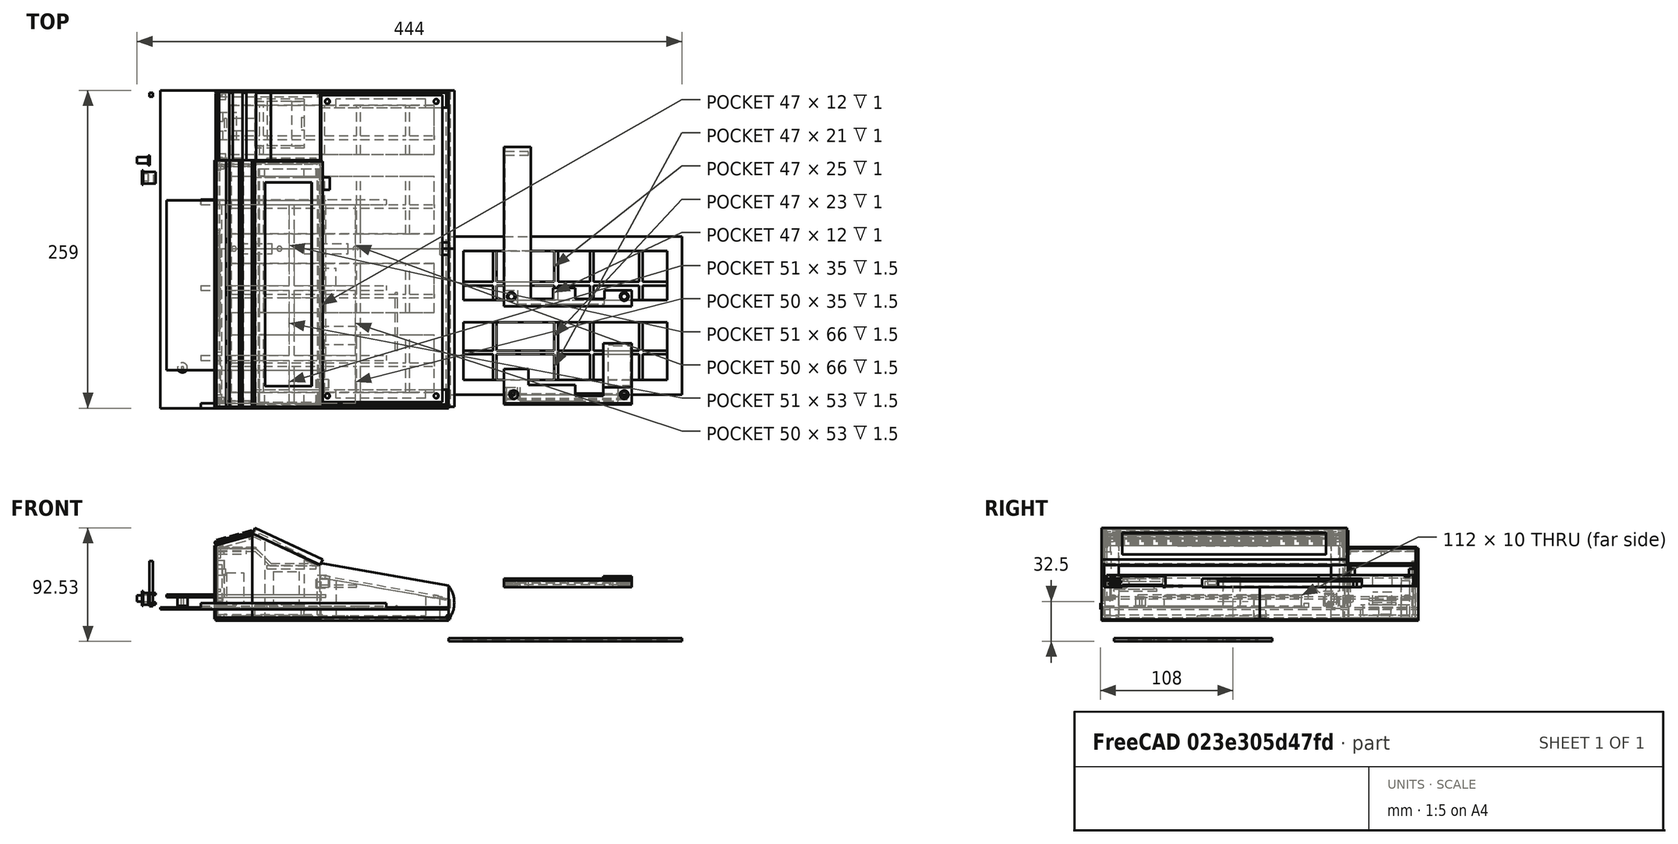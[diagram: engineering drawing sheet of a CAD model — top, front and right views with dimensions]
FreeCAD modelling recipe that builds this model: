
FCSTD DOCUMENT  (FreeCAD 0.20R29603 (Git))
Label: megav2
License: All rights reserved
LicenseURL: http://en.wikipedia.org/wiki/All_rights_reserved
objects: Part::Box×199, Part::Cut×81, Part::Cylinder×32, Part::MultiFuse×26, App::DocumentObjectGroup×14, Part::FeaturePython×1
note: 339 computed .brp shape members not serialized (recipe doc carries the construction recipe); baked Part::Feature solids carry a one-line shape summary decoded from their .brp

FEATURE [Part::Box] Box  label="5x50Keyboard"
  AttacherType = Attacher::AttachEngine3D
  Height = 2
  Length = 100
  Width = 250
FEATURE [Part::Box] Box001  label="MainBoardPCB"
  AttacherType = Attacher::AttachEngine3D
  Height = 2
  Length = 130
  Placement = pos=(-125,28,-8) rot=(0,0,1;0rad)
  Width = 138.5
FEATURE [Part::Box] Box002  label="4x40lcd"
  AttacherType = Attacher::AttachEngine3D
  Height = 2
  Length = 54
  Placement = pos=(-56,2,30) rot=(0,1,0;0.296706rad)
  Width = 190
FEATURE [Part::Box] Box050  label="Cube028"
  AttacherType = Attacher::AttachEngine3D
  Height = 9.5
  Length = 11
  Placement = pos=(0,0,35) rot=(0,0,1;0rad)
  Width = 9.5
FEATURE [Part::Box] Box051  label="Cube029"
  AttacherType = Attacher::AttachEngine3D
  Height = 12
  Length = 1
  Placement = pos=(0,-1,34) rot=(0,0,1;0rad)
  Width = 12
FEATURE [Part::Box] Box052  label="Cube030"
  AttacherType = Attacher::AttachEngine3D
  Height = 7.5
  Length = 4.5
  Placement = pos=(5,-1,36) rot=(0,0,1;0rad)
  Width = 13
FEATURE [Part::Box] Box053  label="Cube031"
  AttacherType = Attacher::AttachEngine3D
  Height = 6
  Length = 4.5
  Placement = pos=(9,-1,36.75) rot=(0,0,1;0rad)
  Width = 13
FEATURE [Part::Cylinder] Cylinder008
  Angle = 360
  AttacherType = Attacher::AttachEngine3D
  FirstAngle = 0
  Height = 9
  Placement = pos=(-1,5,40) rot=(0,1,0;1.5708rad)
  Radius = 3
  SecondAngle = 0
FEATURE [Part::MultiFuse] Fusion010
  Shapes = -> [Box050,Box051]
FEATURE [Part::Cut] Cut016
  Base = -> Fusion010
  Tool = -> Cylinder008
FEATURE [Part::Cut] Cut017
  Base = -> Cut016
  Tool = -> Box052
FEATURE [Part::Cut] Cut018
  Base = -> Cut017
  Placement = pos=(-145,180,-49) rot=(0,0,1;0rad)
  Tool = -> Box053
FEATURE [App::DocumentObjectGroup] Group007  label="resetbutton-case"
  Group = -> [Cut018]
FEATURE [Part::Box] Box054  label="Cube002"
  AttacherType = Attacher::AttachEngine3D
  Height = 60
  Length = 1.5
  Placement = pos=(0,0,-19.5) rot=(0,0,1;0rad)
  Width = 194
FEATURE [Part::Box] Box004  label="Cube003"
  AttacherType = Attacher::AttachEngine3D
  Height = 10
  Length = 10
  Placement = pos=(-3,48,-10) rot=(0,0,1;0rad)
  Width = 112
FEATURE [Part::Box] Box021  label="reset"
  AttacherType = Attacher::AttachEngine3D
  Height = 10
  Length = 10
  Placement = pos=(-2,175,0) rot=(0,0,1;0rad)
  Width = 10
FEATURE [Part::Box] Box025  label="Cube004"
  AttacherType = Attacher::AttachEngine3D
  Height = 5
  Length = 4
  Placement = pos=(1,0,35.5) rot=(0,0,1;0rad)
  Width = 4
FEATURE [Part::Box] Box026  label="Cube005"
  AttacherType = Attacher::AttachEngine3D
  Height = 10
  Length = 4
  Placement = pos=(1,190,30.5) rot=(0,0,1;0rad)
  Width = 4
FEATURE [Part::Cylinder] Cylinder004  label="pwrjack"
  Angle = 360
  AttacherType = Attacher::AttachEngine3D
  FirstAngle = 0
  Height = 10
  Placement = pos=(-3,17,3) rot=(0,1,0;1.5708rad)
  Radius = 3.5
  SecondAngle = 0
FEATURE [Part::Box] Box055  label="Cube032"
  AttacherType = Attacher::AttachEngine3D
  Height = 5.5
  Length = 1.5
  Placement = pos=(7,1,37) rot=(0,0,1;0rad)
  Width = 8
FEATURE [Part::Cylinder] Cylinder009
  Angle = 360
  AttacherType = Attacher::AttachEngine3D
  FirstAngle = 0
  Height = 10
  Placement = pos=(-2,5,40) rot=(0,1,0;1.5708rad)
  Radius = 2.5
  SecondAngle = 0
FEATURE [Part::MultiFuse] Fusion012
  Placement = pos=(-147,194,-49) rot=(0,0,1;0rad)
  Shapes = -> [Cylinder009,Box055]
FEATURE [App::DocumentObjectGroup] Group008  label="resetbutton"
  Group = -> [Fusion012]
FEATURE [Part::Box] Box056  label="base"
  AttacherType = Attacher::AttachEngine3D
  Height = 1.5
  Length = 235
  Placement = pos=(-25,0,-10) rot=(1,0,0;0rad)
  Width = 259
FEATURE [Part::Box] Box027  label="Cube006"
  AttacherType = Attacher::AttachEngine3D
  Height = 4
  Length = 151
  Placement = pos=(8,0,-9) rot=(0,0,1;0rad)
  Width = 4
FEATURE [Part::Box] Box028  label="Cube007"
  AttacherType = Attacher::AttachEngine3D
  Height = 4
  Length = 151
  Placement = pos=(8,166,-9) rot=(0,0,1;0rad)
  Width = 4
FEATURE [Part::Box] Box029  label="Face003"
  AttacherType = Attacher::AttachEngine3D
  Height = 55
  Length = 2
  Placement = pos=(169.2,0,-11) rot=(0,-1,0;0.261799rad)
  Width = 254
FEATURE [Part::Box] Box036  label="Cube014"
  AttacherType = Attacher::AttachEngine3D
  Height = 2
  Length = 151
  Placement = pos=(8,96,-9) rot=(0,0,1;0rad)
  Width = 4
FEATURE [Part::Box] Box037  label="Cube015"
  AttacherType = Attacher::AttachEngine3D
  Height = 2
  Length = 151
  Placement = pos=(8,39,-9) rot=(0,0,1;0rad)
  Width = 4
FEATURE [Part::Box] Box038  label="Cube016"
  AttacherType = Attacher::AttachEngine3D
  Height = 2
  Length = 170
  Placement = pos=(29,0,-9) rot=(0,0,1;1.5708rad)
  Width = 4
FEATURE [Part::Box] Box039  label="Cube017"
  AttacherType = Attacher::AttachEngine3D
  Height = 2
  Length = 170
  Placement = pos=(84,0,-9) rot=(0,0,1;1.5708rad)
  Width = 4
FEATURE [Part::Box] Box040  label="Cube018"
  AttacherType = Attacher::AttachEngine3D
  Height = 2
  Length = 170
  Placement = pos=(138,0,-9) rot=(0,0,1;1.5708rad)
  Width = 4
FEATURE [Part::Cylinder] Cylinder007
  Angle = 360
  AttacherType = Attacher::AttachEngine3D
  FirstAngle = 0
  Height = 47
  Placement = pos=(167.4,94,-8.1) rot=(1,0,0;1.5708rad)
  Radius = 1
  SecondAngle = 0
FEATURE [Part::MultiFuse] Fusion005
  Shapes = -> [Box027,Box028]
FEATURE [Part::Cut] Cut009
  Base = -> Fusion005
  Tool = -> Box029
FEATURE [Part::MultiFuse] Fusion006
  Placement = pos=(-105,-3,-8) rot=(0,0,1;0rad)
  Refine = true
  Shapes = -> [Cut009,Cylinder007,Box036,Box037,Box038,Box039,Box040,Box056]
FEATURE [App::DocumentObjectGroup] Group009  label="CaseBaseold"
  Group = -> [Fusion006]
FEATURE [Part::FeaturePython] Tube002  label="PCBFoot"  # WARN: FeaturePython — macro-defined, semantics opaque (R4)
  AttacherType = Attacher::AttachEngine3D
  Height = 7
  InnerRadius = 1
  OuterRadius = 4
  Placement = pos=(-112,30,-15) rot=(0,0,1;0rad)
FEATURE [Part::Cylinder] Cylinder010
  Angle = 360
  AttacherType = Attacher::AttachEngine3D
  FirstAngle = 0
  Height = 20
  Placement = pos=(5,5,-2) rot=(0,0,1;0rad)
  Radius = 2
  SecondAngle = 0
FEATURE [Part::Cylinder] Cylinder011
  Angle = 360
  AttacherType = Attacher::AttachEngine3D
  FirstAngle = 0
  Height = 20
  Placement = pos=(5,245,-2) rot=(0,0,1;0rad)
  Radius = 2
  SecondAngle = 0
FEATURE [Part::Cylinder] Cylinder012
  Angle = 360
  AttacherType = Attacher::AttachEngine3D
  FirstAngle = 0
  Height = 20
  Placement = pos=(95,245,-2) rot=(0,0,1;0rad)
  Radius = 2
  SecondAngle = 0
FEATURE [Part::Cylinder] Cylinder013
  Angle = 360
  AttacherType = Attacher::AttachEngine3D
  FirstAngle = 0
  Height = 20
  Placement = pos=(95,5,-2) rot=(0,0,1;0rad)
  Radius = 2
  SecondAngle = 0
FEATURE [Part::Cut] Cut019
  Base = -> Box
  Tool = -> Cylinder010
FEATURE [Part::Cut] Cut020
  Base = -> Cut019
  Tool = -> Cylinder011
FEATURE [Part::Cut] Cut021
  Base = -> Cut020
  Tool = -> Cylinder012
FEATURE [Part::Cut] Cut022
  Base = -> Cut021
  Placement = pos=(0,2,5) rot=(0,0,1;0rad)
  Tool = -> Cylinder013
FEATURE [Part::MultiFuse] Fusion
  Placement = pos=(0,0,3) rot=(0,1,0;0.174533rad)
  Shapes = -> [Box002,Cut022]
FEATURE [App::DocumentObjectGroup] Group  label="PCB"
  Group = -> [Box001,Fusion]
FEATURE [Part::Box] Box057  label="pil1"
  AttacherType = Attacher::AttachEngine3D
  Height = 35
  Length = 105
  Placement = pos=(0,-2,-27) rot=(0,0,1;0rad)
  Width = 14
FEATURE [Part::Box] Box058  label="Cube033"
  AttacherType = Attacher::AttachEngine3D
  Height = 41
  Length = 116
  Placement = pos=(-1,-5,8) rot=(0,1,0;0.174533rad)
  Width = 17
FEATURE [Part::Cut] Cut023  label="leftpailslanted"
  Base = -> Box057
  Placement = pos=(0,-1,0) rot=(0,0,1;0rad)
  Tool = -> Box058
FEATURE [Part::Box] Box059  label="pil002"
  AttacherType = Attacher::AttachEngine3D
  Height = 38
  Length = 105
  Placement = pos=(0,-2,-15) rot=(0,0,1;0rad)
  Width = 2
FEATURE [Part::Box] Box060  label="Cube034"
  AttacherType = Attacher::AttachEngine3D
  Height = 41
  Length = 116
  Placement = pos=(-1,-5,18) rot=(0,1,0;0.174533rad)
  Width = 17
FEATURE [Part::Cut] Cut024  label="leftpailslanted001"
  Base = -> Box059
  Placement = pos=(0,-1,2) rot=(0,0,1;0rad)
  Tool = -> Box060
FEATURE [Part::Box] Box061  label="leftpilstop"
  AttacherType = Attacher::AttachEngine3D
  Height = 6
  Length = 2
  Placement = pos=(103,-3,-15) rot=(0,0,1;0rad)
  Width = 14
FEATURE [Part::Box] Box062  label="leftpilsfillremove"
  AttacherType = Attacher::AttachEngine3D
  Height = 46
  Length = 73
  Placement = pos=(13,4,-23) rot=(0,0,1;0rad)
  Width = 10
FEATURE [Part::MultiFuse] Fusion013
  Shapes = -> [Cut023,Cut024,Box061]
FEATURE [Part::Cut] Cut027  label="LeftPillar"
  Base = -> Fusion013
  Tool = -> Box062
FEATURE [Part::Box] Box069  label="lcdpillar"
  AttacherType = Attacher::AttachEngine3D
  Height = 68
  Length = 55
  Placement = pos=(-55,-3,-25) rot=(0,0,1;0rad)
  Width = 14
FEATURE [Part::Box] Box070  label="lcdpillar001slant"
  AttacherType = Attacher::AttachEngine3D
  Height = 58
  Length = 78
  Placement = pos=(-64,-6,48) rot=(0,1,0;0.436332rad)
  Width = 18
FEATURE [Part::Box] Box071  label="lcdpillar001slant001edge"
  AttacherType = Attacher::AttachEngine3D
  Height = 58
  Length = 78
  Placement = pos=(-64,-1,46) rot=(0,1,0;0.436332rad)
  Width = 18
FEATURE [Part::Cut] Cut029
  Base = -> Box069
  Tool = -> Box070
FEATURE [Part::Cut] Cut030
  Base = -> Cut029
  Tool = -> Box071
FEATURE [Part::Box] Box072  label="lcdstopleft"
  AttacherType = Attacher::AttachEngine3D
  Height = 9
  Length = 3
  Placement = pos=(-3,-3,10) rot=(0,0,1;0rad)
  Width = 14
FEATURE [Part::Box] Box073  label="lcdremove"
  AttacherType = Attacher::AttachEngine3D
  Height = 78
  Length = 32
  Placement = pos=(-45,-1,-23) rot=(0,0,1;0rad)
  Width = 17
FEATURE [Part::MultiFuse] Fusion015
  Shapes = -> [Cut030,Box072]
FEATURE [Part::Cut] Cut031  label="leftlcdpillar"
  Base = -> Fusion015
  Tool = -> Box073
FEATURE [Part::Box] Box080  label="lcdpillar002"
  AttacherType = Attacher::AttachEngine3D
  Height = 70
  Length = 55
  Placement = pos=(-55,-3,-26) rot=(0,0,1;0rad)
  Width = 14
FEATURE [Part::Box] Box081  label="lcdpillar001slant002"
  AttacherType = Attacher::AttachEngine3D
  Height = 58
  Length = 78
  Placement = pos=(-64,-6,48) rot=(0,1,0;0.436332rad)
  Width = 18
FEATURE [Part::Box] Box082  label="lcdpillar001slant001edge002"
  AttacherType = Attacher::AttachEngine3D
  Height = 58
  Length = 78
  Placement = pos=(-64,-10,46) rot=(0,1,0;0.436332rad)
  Width = 18
FEATURE [Part::Box] Box084  label="lcdremove002"
  AttacherType = Attacher::AttachEngine3D
  Height = 63
  Length = 32
  Placement = pos=(-45,-9,-17) rot=(0,0,1;0rad)
  Width = 17
FEATURE [Part::Cut] Cut035
  Base = -> Box080
  Tool = -> Box081
FEATURE [Part::Cut] Cut036
  Base = -> Cut035
  Tool = -> Box082
FEATURE [Part::MultiFuse] Fusion019  label="keyboardlcdleftpillar"
  Placement = pos=(0,1,0) rot=(0,0,1;0rad)
  Shapes = -> [Cut027,Cut031]
FEATURE [Part::Box] Box090  label="extcartslot"
  AttacherType = Attacher::AttachEngine3D
  Height = 77
  Length = 30
  Placement = pos=(-130,-3,-37) rot=(0,0,1;0rad)
  Width = 3
FEATURE [Part::Box] Box091  label="Cube039"
  AttacherType = Attacher::AttachEngine3D
  Height = 41
  Length = 107
  Placement = pos=(-150,-8,16.5) rot=(0,-1,0;0.272271rad)
  Width = 10
FEATURE [Part::Cut] Cut041
  Base = -> Box090
  Tool = -> Box091
FEATURE [Part::Box] Box093  label="Cube041"
  AttacherType = Attacher::AttachEngine3D
  Height = 37
  Length = 5
  Placement = pos=(-128,0,-20) rot=(0,0,1;0rad)
  Width = 5
FEATURE [Part::MultiFuse] Fusion021  label="LeftExtCartSlot"
  Placement = pos=(45,1,12) rot=(0,0,1;0rad)
  Shapes = -> [Cut041,Box093]
FEATURE [Part::Box] Box094  label="extcartslot001"
  AttacherType = Attacher::AttachEngine3D
  Height = 73
  Length = 30
  Placement = pos=(-85,-3,-27) rot=(0,0,1;0rad)
  Width = 3
FEATURE [Part::Box] Box095  label="Cube042"
  AttacherType = Attacher::AttachEngine3D
  Height = 51
  Length = 107
  Placement = pos=(-150,-8,17.5) rot=(0,-1,0;0.272271rad)
  Width = 10
FEATURE [Part::Box] Box097  label="Cube044"
  AttacherType = Attacher::AttachEngine3D
  Height = 37
  Length = 5
  Placement = pos=(-83,-7,-15) rot=(0,0,1;0rad)
  Width = 5
FEATURE [Part::Cut] Cut042
  Base = -> Box094
  Tool = -> Box095
FEATURE [Part::MultiFuse] Fusion022  label="RightExtCartSlot001"
  Placement = pos=(0,209.01,0) rot=(0,0,1;0rad)
  Shapes = -> [Cut042,Box097]
FEATURE [Part::Box] Box098  label="Lid"
  AttacherType = Attacher::AttachEngine3D
  Height = 1.5
  Length = 31
  Placement = pos=(-82,-4,22) rot=(0,1,0;0rad)
  Width = 201
FEATURE [Part::Box] Box099  label="LidRib1"
  AttacherType = Attacher::AttachEngine3D
  Height = 1
  Length = 2
  Placement = pos=(-130,-3,61) rot=(0,-1,0;0rad)
  Width = 199
FEATURE [Part::Box] Box100  label="LidRib002"
  AttacherType = Attacher::AttachEngine3D
  Height = 1
  Length = 2
  Placement = pos=(-120,-3,61) rot=(0,-1,0;0rad)
  Width = 199
FEATURE [Part::Box] Box101  label="LidRib003"
  AttacherType = Attacher::AttachEngine3D
  Height = 1
  Length = 2
  Placement = pos=(-110,-3,61) rot=(0,-1,0;0rad)
  Width = 199
FEATURE [Part::Box] Box102  label="LidRib004"
  AttacherType = Attacher::AttachEngine3D
  Height = 1
  Length = 2
  Placement = pos=(-100,-3,61) rot=(0,-1,0;0rad)
  Width = 199
FEATURE [Part::Box] Box103  label="LidRib005"
  AttacherType = Attacher::AttachEngine3D
  Height = 1
  Length = 2
  Placement = pos=(-90,-3,61) rot=(0,-1,0;0rad)
  Width = 199
FEATURE [Part::Box] Box104  label="LidRib006"
  AttacherType = Attacher::AttachEngine3D
  Height = 1
  Length = 2
  Placement = pos=(-80,-7,61) rot=(0,-1,0;0rad)
  Width = 207
FEATURE [Part::Box] Box105  label="LidRib007"
  AttacherType = Attacher::AttachEngine3D
  Height = 1
  Length = 2
  Placement = pos=(-70,-7,61) rot=(0,-1,0;0rad)
  Width = 211
FEATURE [Part::Box] Box106  label="LidRib008"
  AttacherType = Attacher::AttachEngine3D
  Height = 1
  Length = 2
  Placement = pos=(-60,-4,61) rot=(0,-1,0;0rad)
  Width = 205
FEATURE [Part::Box] Box107  label="Cube045"
  AttacherType = Attacher::AttachEngine3D
  Height = 2
  Length = 28
  Placement = pos=(-79,-1,20) rot=(0,0,1;0rad)
  Width = 2
FEATURE [Part::Box] Box108  label="Cube046"
  AttacherType = Attacher::AttachEngine3D
  Height = 2
  Length = 28
  Placement = pos=(-79,192,20) rot=(0,0,1;0rad)
  Width = 2
FEATURE [Part::Box] Box109  label="Cube047"
  AttacherType = Attacher::AttachEngine3D
  Height = 2
  Length = 2
  Placement = pos=(-80,60,20) rot=(0,0,1;0rad)
  Width = 80
FEATURE [Part::MultiFuse] Fusion023  label="Lid001"
  Placement = pos=(0,0,38) rot=(0,1,0;0rad)
  Shapes = -> [Box098,Box107,Box108,Box109]
FEATURE [Part::Cut] Cut043
  Base = -> Fusion023
  Tool = -> Box099
FEATURE [Part::Cut] Cut044
  Base = -> Cut043
  Tool = -> Box100
FEATURE [Part::Cut] Cut045
  Base = -> Cut044
  Tool = -> Box101
FEATURE [Part::Cut] Cut046
  Base = -> Cut045
  Tool = -> Box102
FEATURE [Part::Cut] Cut047
  Base = -> Cut046
  Tool = -> Box103
FEATURE [Part::Cut] Cut048
  Base = -> Cut047
  Tool = -> Box104
FEATURE [Part::Cut] Cut049
  Base = -> Cut048
  Tool = -> Box105
FEATURE [Part::Cut] Cut050  label="Lid002"
  Base = -> Cut049
  Placement = pos=(10,2,0) rot=(0,-1,0;0.272271rad)
  Tool = -> Box106
FEATURE [Part::Box] Box111  label="Cube049"
  AttacherType = Attacher::AttachEngine3D
  Height = 25
  Length = 14
  Placement = pos=(-76,203,-13) rot=(0,0,1;0rad)
  Width = 10
FEATURE [Part::Cut] Cut052  label="RightExtCartSlotWithHole"
  Base = -> Fusion022
  Placement = pos=(0,-10,0) rot=(0,0,1;0rad)
  Tool = -> Box111
FEATURE [Part::Box] Box112  label="Cube050"
  AttacherType = Attacher::AttachEngine3D
  Height = 2
  Length = 104
  Placement = pos=(150,0,0) rot=(0,0,1;0rad)
  Width = 8
FEATURE [Part::Box] Box113  label="Cube051"
  AttacherType = Attacher::AttachEngine3D
  Height = 5.6
  Length = 104
  Placement = pos=(150,0,0) rot=(0,0,1;0rad)
  Width = 4
FEATURE [Part::Box] Box114  label="Cube052"
  AttacherType = Attacher::AttachEngine3D
  Height = 2
  Length = 104
  Placement = pos=(150,0,3.6) rot=(0,0,1;0rad)
  Width = 8
FEATURE [Part::Box] Box115  label="Cube053"
  AttacherType = Attacher::AttachEngine3D
  Height = 2
  Length = 11
  Placement = pos=(150,4,0) rot=(0,0,1;0rad)
  Width = 10
FEATURE [Part::Cylinder] Cylinder
  Angle = 360
  AttacherType = Attacher::AttachEngine3D
  FirstAngle = 0
  Height = 10
  Placement = pos=(156,9,-3) rot=(0,0,1;0rad)
  Radius = 2.5
  SecondAngle = 0
FEATURE [Part::Box] Box116  label="Cube054"
  AttacherType = Attacher::AttachEngine3D
  Height = 2
  Length = 11
  Placement = pos=(150,4,3.6) rot=(0,0,1;0rad)
  Width = 10
FEATURE [Part::Box] Box117  label="Cube055"
  AttacherType = Attacher::AttachEngine3D
  Height = 2
  Length = 11
  Placement = pos=(243,4,3.6) rot=(0,0,1;0rad)
  Width = 10
FEATURE [Part::Box] Box118  label="Cube056"
  AttacherType = Attacher::AttachEngine3D
  Height = 2
  Length = 11
  Placement = pos=(243,4,0) rot=(0,0,1;0rad)
  Width = 10
FEATURE [Part::Cylinder] Cylinder014
  Angle = 360
  AttacherType = Attacher::AttachEngine3D
  FirstAngle = 0
  Height = 10
  Placement = pos=(248,9,-3) rot=(0,0,1;0rad)
  Radius = 2.5
  SecondAngle = 0
FEATURE [Part::MultiFuse] Fusion024
  Shapes = -> [Box112,Box113,Box114,Box115,Box116,Box117,Box118]
FEATURE [Part::Cut] Cut053
  Base = -> Fusion024
  Tool = -> Cylinder014
FEATURE [Part::Cut] Cut054  label="KeyBoardRiser"
  Base = -> Cut053
  Tool = -> Cylinder
FEATURE [Part::Box] Box083  label="lcdstopleft002"
  AttacherType = Attacher::AttachEngine3D
  Height = 9
  Length = 3
  Placement = pos=(-3,-3,10) rot=(0,0,1;0rad)
  Width = 14
FEATURE [Part::MultiFuse] Fusion017
  Shapes = -> [Cut036,Box083]
FEATURE [Part::Cut] Cut037  label="rightlcdpillar002"
  Base = -> Fusion017
  Placement = pos=(0,188,0) rot=(0,0,1;0rad)
  Tool = -> Box084
FEATURE [Part::Box] Box143  label="NewBasePanel008"
  AttacherType = Attacher::AttachEngine3D
  Height = 2.5
  Length = 190
  Placement = pos=(105,8,-45) rot=(0,0,1;0rad)
  Width = 129
FEATURE [Part::Box] Box144  label="NewBasePanel009"
  AttacherType = Attacher::AttachEngine3D
  Height = 2.5
  Length = 166
  Placement = pos=(117,20,-44) rot=(0,0,1;0rad)
  Width = 105
FEATURE [Part::Box] Box145  label="Cube072"
  AttacherType = Attacher::AttachEngine3D
  Height = 1
  Length = 184
  Placement = pos=(105,41,-43) rot=(0,0,1;0rad)
  Width = 3
FEATURE [Part::Box] Box146  label="Cube073"
  AttacherType = Attacher::AttachEngine3D
  Height = 1
  Length = 184.5
  Placement = pos=(105,97,-43) rot=(0,0,1;0rad)
  Width = 3
FEATURE [Part::Box] Box147  label="Cube074"
  AttacherType = Attacher::AttachEngine3D
  Height = 1
  Length = 3
  Placement = pos=(141,8,-43) rot=(0,0,1;0rad)
  Width = 129
FEATURE [Part::Box] Box148  label="Cube075"
  AttacherType = Attacher::AttachEngine3D
  Height = 1
  Length = 3
  Placement = pos=(191,8,-43) rot=(0,0,1;0rad)
  Width = 129
FEATURE [Part::Cut] Cut059
  Base = -> Box143
  Placement = pos=(0,0,1) rot=(0,0,1;0rad)
  Tool = -> Box144
FEATURE [Part::Box] Box149  label="Cube076"
  AttacherType = Attacher::AttachEngine3D
  Height = 1.5
  Length = 186.5
  Placement = pos=(105,67,-43) rot=(0,0,1;0rad)
  Width = 18
FEATURE [Part::Box] Box206  label="pil005"
  AttacherType = Attacher::AttachEngine3D
  Height = 25
  Length = 105
  Placement = pos=(0,-2,-15) rot=(0,0,1;0rad)
  Width = 14
FEATURE [Part::Box] Box207  label="Cube117"
  AttacherType = Attacher::AttachEngine3D
  Height = 41
  Length = 116
  Placement = pos=(-1,-5,8) rot=(0,1,0;0.174533rad)
  Width = 17
FEATURE [Part::Cut] Cut068  label="rightpailslanted003"
  Base = -> Box206
  Placement = pos=(0,99,0) rot=(0,0,1;0rad)
  Tool = -> Box207
FEATURE [Part::Box] Box208  label="Cube"
  AttacherType = Attacher::AttachEngine3D
  Height = 25
  Length = 120
  Placement = pos=(13,95,-18) rot=(0,0,1;0rad)
  Width = 23
FEATURE [Part::Cut] Cut069  label="keyboardcentrepillar"
  Base = -> Cut068
  Tool = -> Box208
FEATURE [App::DocumentObjectGroup] Group010  label="KeyboardPillars"
  Group = -> [Cut069]
FEATURE [Part::Box] Box209  label="LinkPlate"
  AttacherType = Attacher::AttachEngine3D
  Height = 2
  Length = 30
  Placement = pos=(0,49,0) rot=(0,0,1;0rad)
  Width = 15
FEATURE [Part::Box] Box210  label="Cube118"
  AttacherType = Attacher::AttachEngine3D
  Height = 37
  Length = 130
  Placement = pos=(-40,201,19.5) rot=(0,-1,0;0.785398rad)
  Width = 54
FEATURE [Part::Box] Box211  label="Cube119"
  AttacherType = Attacher::AttachEngine3D
  Height = 57
  Length = 85
  Placement = pos=(-85,202,-25) rot=(0,0,1;0rad)
  Width = 2
FEATURE [Part::Box] Box212  label="Cube120"
  AttacherType = Attacher::AttachEngine3D
  Height = 37
  Length = 130
  Placement = pos=(-40,201,19.5) rot=(0,0,1;0rad)
  Width = 54
FEATURE [Part::Cut] Cut070
  Base = -> Box211
  Tool = -> Box210
FEATURE [Part::Cut] Cut071  label="BoxPanel"
  Base = -> Cut070
  Placement = pos=(0,53,0) rot=(0,0,1;0rad)
  Tool = -> Box212
FEATURE [Part::Box] Box213  label="Cube121"
  AttacherType = Attacher::AttachEngine3D
  Height = 27
  Length = 3
  Placement = pos=(-2,252,-22.5) rot=(0,0,1;0rad)
  Width = 2
FEATURE [Part::Box] Box214  label="Cube122"
  AttacherType = Attacher::AttachEngine3D
  Height = 34
  Length = 3
  Placement = pos=(-83,253,-15.5) rot=(0,0,1;0rad)
  Width = 3
FEATURE [Part::Box] Box215  label="BoxPanelSupports"
  AttacherType = Attacher::AttachEngine3D
  Height = 37
  Length = 3
  Placement = pos=(-139,251,-15.5) rot=(0,0,1;0rad)
  Width = 3
FEATURE [Part::MultiFuse] Fusion039  label="BoxPanelRight"
  Placement = pos=(0,-1,0) rot=(0,0,1;0rad)
  Shapes = -> [Cut071,Box214]
FEATURE [Part::Box] Box216  label="Cube123"
  AttacherType = Attacher::AttachEngine3D
  Height = 37
  Length = 83
  Placement = pos=(-83,199,-15.5) rot=(0,0,1;0rad)
  Width = 55
FEATURE [Part::Box] Box217  label="Cube124"
  AttacherType = Attacher::AttachEngine3D
  Height = 36
  Length = 128
  Placement = pos=(-40,199,9.5) rot=(0,-1,0;0.785398rad)
  Width = 58
FEATURE [Part::Box] Box218  label="Cube125"
  AttacherType = Attacher::AttachEngine3D
  Height = 37
  Length = 75
  Placement = pos=(-128,199,-17.5) rot=(0,0,1;0rad)
  Width = 63
FEATURE [Part::Box] Box219  label="Cube126"
  AttacherType = Attacher::AttachEngine3D
  Height = 36
  Length = 128
  Placement = pos=(-118,198,-96.5) rot=(0,-1,0;0.785398rad)
  Width = 60
FEATURE [Part::Cut] Cut072
  Base = -> Box216
  Tool = -> Box217
FEATURE [Part::Cut] Cut073
  Base = -> Cut072
  Tool = -> Box218
FEATURE [Part::Cut] Cut074
  Base = -> Cut073
  Tool = -> Box219
FEATURE [Part::Box] Box220  label="Cube127"
  AttacherType = Attacher::AttachEngine3D
  Height = 37
  Length = 75
  Placement = pos=(-75,199,-29.5) rot=(0,0,1;0rad)
  Width = 63
FEATURE [Part::Box] Box221  label="Cube128"
  AttacherType = Attacher::AttachEngine3D
  Height = 37
  Length = 75
  Placement = pos=(-40,199,9.5) rot=(0,0,1;0rad)
  Width = 63
FEATURE [Part::Cut] Cut075
  Base = -> Cut074
  Tool = -> Box220
FEATURE [Part::Cut] Cut076  label="BoxLidShape"
  Base = -> Cut075
  Tool = -> Box221
FEATURE [Part::Box] Box225  label="BoxPanelSupports004"
  AttacherType = Attacher::AttachEngine3D
  Height = 56
  Length = 8
  Placement = pos=(-60,255,21.5) rot=(1,0,0;1.5708rad)
  Width = 1.5
FEATURE [Part::Box] Box228  label="BoxPanelSupports007"
  AttacherType = Attacher::AttachEngine3D
  Height = 56
  Length = 8
  Placement = pos=(-82,255,21.5) rot=(1,0,0;1.5708rad)
  Width = 1.5
FEATURE [Part::Box] Box229  label="BoxPanelSupports008"
  AttacherType = Attacher::AttachEngine3D
  Height = 56
  Length = 8
  Placement = pos=(-71,255,21.5) rot=(1,0,0;1.5708rad)
  Width = 1.5
FEATURE [Part::MultiFuse] Fusion040  label="BoxLid"
  Placement = pos=(0,0,10) rot=(0,0,1;0rad)
  Shapes = -> [Cut076,Box225,Box228,Box229]
FEATURE [Part::Box] Box232  label="lcdbezelouter"
  AttacherType = Attacher::AttachEngine3D
  Height = 5
  Length = 61
  Placement = pos=(-55,-2,44) rot=(0,1,0;0.436332rad)
  Width = 200
FEATURE [Part::Box] Box233  label="Cube129"
  AttacherType = Attacher::AttachEngine3D
  Height = 10
  Length = 42
  Placement = pos=(-46,15,42) rot=(0,1,0;0.436332rad)
  Width = 166
FEATURE [Part::Cut] Cut077
  Base = -> Box232
  Tool = -> Box233
FEATURE [Part::Box] Box234  label="lcdbezelouter001"
  AttacherType = Attacher::AttachEngine3D
  Height = 5
  Length = 58
  Placement = pos=(-54,0,42) rot=(0,1,0;0.436332rad)
  Width = 196
FEATURE [Part::Cut] Cut078  label="LcdBezel"
  Base = -> Cut077
  Tool = -> Box234
FEATURE [Part::Box] Box235  label="Cube130"
  AttacherType = Attacher::AttachEngine3D
  Height = 2
  Length = 104
  Placement = pos=(150,1,0) rot=(0,0,1;0rad)
  Width = 8
FEATURE [Part::Box] Box236  label="Cube131"
  AttacherType = Attacher::AttachEngine3D
  Height = 5.6
  Length = 104
  Placement = pos=(150,1,0) rot=(0,0,1;0rad)
  Width = 4
FEATURE [Part::Box] Box237  label="Cube132"
  AttacherType = Attacher::AttachEngine3D
  Height = 2
  Length = 104
  Placement = pos=(150,1,3.6) rot=(0,0,1;0rad)
  Width = 8
FEATURE [Part::Box] Box238  label="Cube133"
  AttacherType = Attacher::AttachEngine3D
  Height = 2
  Length = 11
  Placement = pos=(150,4,0) rot=(0,0,1;0rad)
  Width = 10
FEATURE [Part::Box] Box239  label="Cube134"
  AttacherType = Attacher::AttachEngine3D
  Height = 2
  Length = 11
  Placement = pos=(150,4,3.6) rot=(0,0,1;0rad)
  Width = 10
FEATURE [Part::Box] Box240  label="Cube135"
  AttacherType = Attacher::AttachEngine3D
  Height = 2
  Length = 11
  Placement = pos=(243,4,3.6) rot=(0,0,1;0rad)
  Width = 10
FEATURE [Part::Box] Box241  label="Cube136"
  AttacherType = Attacher::AttachEngine3D
  Height = 2
  Length = 11
  Placement = pos=(243,4,0) rot=(0,0,1;0rad)
  Width = 10
FEATURE [Part::Cylinder] Cylinder015
  Angle = 360
  AttacherType = Attacher::AttachEngine3D
  FirstAngle = 0
  Height = 10
  Placement = pos=(156,9,-3) rot=(0,0,1;0rad)
  Radius = 2.5
  SecondAngle = 0
FEATURE [Part::Cylinder] Cylinder016
  Angle = 360
  AttacherType = Attacher::AttachEngine3D
  FirstAngle = 0
  Height = 10
  Placement = pos=(248,9,-3) rot=(0,0,1;0rad)
  Radius = 2.5
  SecondAngle = 0
FEATURE [Part::MultiFuse] Fusion041
  Shapes = -> [Box235,Box236,Box237,Box238,Box239,Box240,Box241]
FEATURE [Part::Cut] Cut079
  Base = -> Fusion041
  Tool = -> Cylinder016
FEATURE [Part::Cut] Cut080  label="KeyBoardRiser001"
  Base = -> Cut079
  Tool = -> Cylinder015
FEATURE [Part::Box] Box243  label="Cube138"
  AttacherType = Attacher::AttachEngine3D
  Height = 7
  Length = 104
  Placement = pos=(150,1,0) rot=(0,0,1;0rad)
  Width = 2
FEATURE [Part::Box] Box244  label="Cube139"
  AttacherType = Attacher::AttachEngine3D
  Height = 2
  Length = 104
  Placement = pos=(150,1,5) rot=(0,0,1;0rad)
  Width = 6
FEATURE [Part::Box] Box246  label="Cube141"
  AttacherType = Attacher::AttachEngine3D
  Height = 7
  Length = 11
  Placement = pos=(150,2,0) rot=(0,0,1;0rad)
  Width = 12
FEATURE [Part::Box] Box247  label="Cube142"
  AttacherType = Attacher::AttachEngine3D
  Height = 7
  Length = 22
  Placement = pos=(232,2,0) rot=(0,0,1;0rad)
  Width = 12
FEATURE [Part::Cylinder] Cylinder017
  Angle = 360
  AttacherType = Attacher::AttachEngine3D
  FirstAngle = 0
  Height = 10
  Placement = pos=(156,9,-3) rot=(0,0,1;0rad)
  Radius = 2.5
  SecondAngle = 0
FEATURE [Part::Cylinder] Cylinder018
  Angle = 360
  AttacherType = Attacher::AttachEngine3D
  FirstAngle = 0
  Height = 10
  Placement = pos=(248,9,-3) rot=(0,0,1;0rad)
  Radius = 2.5
  SecondAngle = 0
FEATURE [Part::Box] Box248  label="Cube143"
  AttacherType = Attacher::AttachEngine3D
  Height = 2
  Length = 22
  Placement = pos=(150,1,5) rot=(0,0,1;0rad)
  Width = 130
FEATURE [Part::Box] Box249  label="Cube144"
  AttacherType = Attacher::AttachEngine3D
  Height = 2
  Length = 18
  Placement = pos=(190,1,5) rot=(0,0,1;0rad)
  Width = 15
FEATURE [Part::Box] Box250  label="Cube145"
  AttacherType = Attacher::AttachEngine3D
  Height = 7
  Length = 1
  Placement = pos=(150,1,0) rot=(0,0,1;0rad)
  Width = 130
FEATURE [Part::Box] Box268  label="Cube163"
  AttacherType = Attacher::AttachEngine3D
  Height = 7
  Length = 104
  Placement = pos=(150,1,0) rot=(0,0,1;0rad)
  Width = 2
FEATURE [Part::Box] Box269  label="Cube164"
  AttacherType = Attacher::AttachEngine3D
  Height = 2
  Length = 104
  Placement = pos=(150,1,5) rot=(0,0,1;0rad)
  Width = 6
FEATURE [Part::Box] Box270  label="Cube165"
  AttacherType = Attacher::AttachEngine3D
  Height = 7
  Length = 11
  Placement = pos=(152,2,0) rot=(0,0,1;0rad)
  Width = 12
FEATURE [Part::Box] Box271  label="Cube166"
  AttacherType = Attacher::AttachEngine3D
  Height = 7
  Length = 11
  Placement = pos=(243,2,0) rot=(0,0,1;0rad)
  Width = 12
FEATURE [Part::Box] Box273  label="Cube168"
  AttacherType = Attacher::AttachEngine3D
  Height = 2
  Length = 57
  Placement = pos=(151,1,5) rot=(0,0,1;0rad)
  Width = 15
FEATURE [Part::Box] Box274  label="Cube169"
  AttacherType = Attacher::AttachEngine3D
  Height = 7
  Length = 1
  Placement = pos=(253,1,0) rot=(0,0,1;0rad)
  Width = 49
FEATURE [Part::Cylinder] Cylinder029
  Angle = 360
  AttacherType = Attacher::AttachEngine3D
  FirstAngle = 0
  Height = 10
  Placement = pos=(158,8,-3) rot=(0,0,1;0rad)
  Radius = 2.5
  SecondAngle = 0
FEATURE [Part::Cylinder] Cylinder030
  Angle = 360
  AttacherType = Attacher::AttachEngine3D
  FirstAngle = 0
  Height = 10
  Placement = pos=(248,8,-3) rot=(0,0,1;0rad)
  Radius = 2.5
  SecondAngle = 0
FEATURE [Part::Box] Box276  label="Cube171"
  AttacherType = Attacher::AttachEngine3D
  Height = 2
  Length = 20
  Placement = pos=(150,1,5) rot=(0,0,1;0rad)
  Width = 28
FEATURE [Part::Box] Box277  label="Cube172"
  AttacherType = Attacher::AttachEngine3D
  Height = 2
  Length = 22
  Placement = pos=(231,1,5) rot=(0,0,1;0rad)
  Width = 13
FEATURE [Part::Box] Box280  label="Cube175"
  AttacherType = Attacher::AttachEngine3D
  Height = 2
  Length = 23
  Placement = pos=(231,14,5) rot=(0,0,1;0rad)
  Width = 36
FEATURE [Part::Box] Box281  label="Cube176"
  AttacherType = Attacher::AttachEngine3D
  Height = 2
  Length = 23
  Placement = pos=(235,15.5,5) rot=(0,0,1;0rad)
  Width = 33
FEATURE [Part::Cut] Cut089
  Base = -> Box280
  Tool = -> Box281
FEATURE [Part::Box] Box282  label="Cube177"
  AttacherType = Attacher::AttachEngine3D
  Height = 1
  Length = 3
  Placement = pos=(220,8,-43) rot=(0,0,1;0rad)
  Width = 129
FEATURE [Part::Box] Box283  label="Cube178"
  AttacherType = Attacher::AttachEngine3D
  Height = 1
  Length = 3
  Placement = pos=(260,8,-43) rot=(0,0,1;0rad)
  Width = 129
FEATURE [Part::MultiFuse] Fusion029  label="NewBasePanelSection"
  Shapes = -> [Cut059,Box145,Box146,Box147,Box148,Box149,Box282,Box283]
FEATURE [Part::Box] Box284  label="NewBasePanel010"
  AttacherType = Attacher::AttachEngine3D
  Height = 2.5
  Length = 190
  Placement = pos=(105,8,-45) rot=(0,0,1;0rad)
  Width = 129
FEATURE [Part::Box] Box285  label="NewBasePanel011"
  AttacherType = Attacher::AttachEngine3D
  Height = 2.5
  Length = 166
  Placement = pos=(117,20,-44) rot=(0,0,1;0rad)
  Width = 105
FEATURE [Part::Box] Box286  label="Cube179"
  AttacherType = Attacher::AttachEngine3D
  Height = 1
  Length = 184
  Placement = pos=(105,41,-43) rot=(0,0,1;0rad)
  Width = 3
FEATURE [Part::Box] Box287  label="Cube180"
  AttacherType = Attacher::AttachEngine3D
  Height = 1
  Length = 184.5
  Placement = pos=(105,97,-43) rot=(0,0,1;0rad)
  Width = 3
FEATURE [Part::Box] Box288  label="Cube181"
  AttacherType = Attacher::AttachEngine3D
  Height = 1
  Length = 3
  Placement = pos=(141,8,-43) rot=(0,0,1;0rad)
  Width = 129
FEATURE [Part::Box] Box289  label="Cube182"
  AttacherType = Attacher::AttachEngine3D
  Height = 1
  Length = 3
  Placement = pos=(191,8,-43) rot=(0,0,1;0rad)
  Width = 129
FEATURE [Part::Box] Box290  label="Cube183"
  AttacherType = Attacher::AttachEngine3D
  Height = 1.5
  Length = 186.5
  Placement = pos=(105,67,-43) rot=(0,0,1;0rad)
  Width = 18
FEATURE [Part::Box] Box291  label="Cube184"
  AttacherType = Attacher::AttachEngine3D
  Height = 1
  Length = 3
  Placement = pos=(220,8,-43) rot=(0,0,1;0rad)
  Width = 129
FEATURE [Part::Box] Box292  label="Cube185"
  AttacherType = Attacher::AttachEngine3D
  Height = 1
  Length = 3
  Placement = pos=(260,8,-43) rot=(0,0,1;0rad)
  Width = 129
FEATURE [Part::Cut] Cut090
  Base = -> Box284
  Placement = pos=(0,0,1) rot=(0,0,1;0rad)
  Tool = -> Box285
FEATURE [Part::MultiFuse] Fusion046  label="NewBasePanelSection001"
  Placement = pos=(-190,-10,17) rot=(0,0,1;0rad)
  Shapes = -> [Cut090,Box286,Box287,Box288,Box289,Box290,Box291,Box292]
FEATURE [Part::Box] Box293  label="NewBasePanel012"
  AttacherType = Attacher::AttachEngine3D
  Height = 2.5
  Length = 190
  Placement = pos=(105,8,-45) rot=(0,0,1;0rad)
  Width = 129
FEATURE [Part::Box] Box294  label="NewBasePanel013"
  AttacherType = Attacher::AttachEngine3D
  Height = 2.5
  Length = 166
  Placement = pos=(117,20,-44) rot=(0,0,1;0rad)
  Width = 105
FEATURE [Part::Box] Box295  label="Cube186"
  AttacherType = Attacher::AttachEngine3D
  Height = 1
  Length = 184
  Placement = pos=(105,41,-43) rot=(0,0,1;0rad)
  Width = 3
FEATURE [Part::Box] Box296  label="Cube187"
  AttacherType = Attacher::AttachEngine3D
  Height = 1
  Length = 184.5
  Placement = pos=(105,97,-43) rot=(0,0,1;0rad)
  Width = 3
FEATURE [Part::Box] Box297  label="Cube188"
  AttacherType = Attacher::AttachEngine3D
  Height = 1
  Length = 3
  Placement = pos=(141,8,-43) rot=(0,0,1;0rad)
  Width = 129
FEATURE [Part::Box] Box298  label="Cube189"
  AttacherType = Attacher::AttachEngine3D
  Height = 1
  Length = 3
  Placement = pos=(191,8,-43) rot=(0,0,1;0rad)
  Width = 129
FEATURE [Part::Box] Box299  label="Cube190"
  AttacherType = Attacher::AttachEngine3D
  Height = 1.5
  Length = 186.5
  Placement = pos=(105,67,-43) rot=(0,0,1;0rad)
  Width = 18
FEATURE [Part::Box] Box300  label="Cube191"
  AttacherType = Attacher::AttachEngine3D
  Height = 1
  Length = 3
  Placement = pos=(220,8,-43) rot=(0,0,1;0rad)
  Width = 129
FEATURE [Part::Box] Box301  label="Cube192"
  AttacherType = Attacher::AttachEngine3D
  Height = 1
  Length = 3
  Placement = pos=(260,8,-43) rot=(0,0,1;0rad)
  Width = 129
FEATURE [Part::Cut] Cut091
  Base = -> Box293
  Placement = pos=(0,0,1) rot=(0,0,1;0rad)
  Tool = -> Box294
FEATURE [Part::MultiFuse] Fusion047  label="NewBasePanelSection002"
  Placement = pos=(-190,119,17) rot=(0,0,1;0rad)
  Shapes = -> [Cut091,Box295,Box296,Box297,Box298,Box299,Box300,Box301]
FEATURE [Part::Cylinder] Cylinder033
  Angle = 360
  AttacherType = Attacher::AttachEngine3D
  FirstAngle = 0
  Height = 129
  Placement = pos=(87,127,-13) rot=(1,0,0;1.5708rad)
  Radius = 23
  SecondAngle = 0
FEATURE [Part::Box] Box302  label="Cube193"
  AttacherType = Attacher::AttachEngine3D
  Height = 57
  Length = 48
  Placement = pos=(57.5,-10,-43) rot=(0,0,1;0rad)
  Width = 155
FEATURE [Part::Cut] Cut092  label="WristRest1"
  Base = -> Cylinder033
  Placement = pos=(-0.5,0,0.5) rot=(0,0,1;0rad)
  Tool = -> Box302
FEATURE [Part::Cylinder] Cylinder034
  Angle = 360
  AttacherType = Attacher::AttachEngine3D
  FirstAngle = 0
  Height = 129
  Placement = pos=(104.5,127,-24) rot=(1,0,0;1.5708rad)
  Radius = 1.5
  SecondAngle = 0
FEATURE [Part::Box] Box303  label="Cube194"
  AttacherType = Attacher::AttachEngine3D
  Height = 57
  Length = 48
  Placement = pos=(57.5,-10,-43) rot=(0,0,1;0rad)
  Width = 155
FEATURE [Part::Cylinder] Cylinder035
  Angle = 360
  AttacherType = Attacher::AttachEngine3D
  FirstAngle = 0
  Height = 129
  Placement = pos=(87,127,-13) rot=(1,0,0;1.5708rad)
  Radius = 23
  SecondAngle = 0
FEATURE [Part::Cut] Cut093  label="WristRest002"
  Base = -> Cylinder035
  Placement = pos=(-0.5,129,0.5) rot=(0,0,1;0rad)
  Tool = -> Box303
FEATURE [Part::Cylinder] Cylinder036
  Angle = 360
  AttacherType = Attacher::AttachEngine3D
  FirstAngle = 0
  Height = 129
  Placement = pos=(104.5,256,-24) rot=(1,0,0;1.5708rad)
  Radius = 1.5
  SecondAngle = 0
FEATURE [Part::Box] Box304  label="pil006"
  AttacherType = Attacher::AttachEngine3D
  Height = 20
  Length = 105
  Placement = pos=(0,-2,-10) rot=(0,0,1;0rad)
  Width = 5
FEATURE [Part::Box] Box305  label="Cube195"
  AttacherType = Attacher::AttachEngine3D
  Height = 41
  Length = 116
  Placement = pos=(-1,-5,8) rot=(0,1,0;0.174533rad)
  Width = 17
FEATURE [Part::Box] Box306  label="Cube196"
  AttacherType = Attacher::AttachEngine3D
  Height = 25
  Length = 120
  Placement = pos=(8,95,-18) rot=(0,0,1;0rad)
  Width = 23
FEATURE [Part::Cut] Cut094  label="rightpailslanted004"
  Base = -> Box304
  Placement = pos=(0,99,0) rot=(0,0,1;0rad)
  Tool = -> Box305
FEATURE [Part::Cut] Cut095  label="keyboardcentrepillar001"
  Base = -> Cut094
  Placement = pos=(98,25,-16) rot=(0,0,1;0rad)
  Tool = -> Box306
FEATURE [Part::Box] Box307  label="pil007"
  AttacherType = Attacher::AttachEngine3D
  Height = 35
  Length = 105
  Placement = pos=(0,-2,-27) rot=(0,0,1;0rad)
  Width = 14
FEATURE [Part::Box] Box308  label="Cube197"
  AttacherType = Attacher::AttachEngine3D
  Height = 41
  Length = 116
  Placement = pos=(-1,-5,8) rot=(0,1,0;0.174533rad)
  Width = 17
FEATURE [Part::Box] Box309  label="pil008"
  AttacherType = Attacher::AttachEngine3D
  Height = 38
  Length = 105
  Placement = pos=(0,-2,-15) rot=(0,0,1;0rad)
  Width = 2
FEATURE [Part::Box] Box310  label="Cube198"
  AttacherType = Attacher::AttachEngine3D
  Height = 41
  Length = 116
  Placement = pos=(-1,-5,18) rot=(0,1,0;0.174533rad)
  Width = 17
FEATURE [Part::Box] Box311  label="leftpilstop001"
  AttacherType = Attacher::AttachEngine3D
  Height = 6
  Length = 2
  Placement = pos=(103,-3,-15) rot=(0,0,1;0rad)
  Width = 14
FEATURE [Part::Box] Box312  label="leftpilsfillremove001"
  AttacherType = Attacher::AttachEngine3D
  Height = 46
  Length = 73
  Placement = pos=(13,-6,-23) rot=(0,0,1;0rad)
  Width = 10
FEATURE [Part::Cut] Cut096  label="leftpailslanted002"
  Base = -> Box307
  Placement = pos=(0,-1,0) rot=(0,0,1;0rad)
  Tool = -> Box308
FEATURE [Part::Cut] Cut097  label="leftpailslanted003"
  Base = -> Box309
  Placement = pos=(0,11,2) rot=(0,0,1;0rad)
  Tool = -> Box310
FEATURE [Part::MultiFuse] Fusion048
  Shapes = -> [Cut096,Cut097,Box311]
FEATURE [Part::Cut] Cut098  label="RightPillar001"
  Base = -> Fusion048
  Placement = pos=(0,245,0) rot=(0,0,1;0rad)
  Tool = -> Box312
FEATURE [Part::Box] Box313  label="pil009"
  AttacherType = Attacher::AttachEngine3D
  Height = 20
  Length = 105
  Placement = pos=(0,-2,-10) rot=(0,0,1;0rad)
  Width = 5
FEATURE [Part::Box] Box314  label="Cube199"
  AttacherType = Attacher::AttachEngine3D
  Height = 41
  Length = 116
  Placement = pos=(-1,-5,8) rot=(0,1,0;0.174533rad)
  Width = 17
FEATURE [Part::Box] Box315  label="Cube200"
  AttacherType = Attacher::AttachEngine3D
  Height = 25
  Length = 120
  Placement = pos=(8,95,-18) rot=(0,0,1;0rad)
  Width = 23
FEATURE [Part::Cut] Cut099  label="rightpailslanted005"
  Base = -> Box313
  Placement = pos=(0,99,0) rot=(0,0,1;0rad)
  Tool = -> Box314
FEATURE [Part::Cut] Cut100  label="keyboardcentrepillar002"
  Base = -> Cut099
  Placement = pos=(98,30,-16) rot=(0,0,1;0rad)
  Tool = -> Box315
FEATURE [App::DocumentObjectGroup] Group014  label="PowerBox"
  Group = -> [Fusion040,Fusion039]
FEATURE [Part::Box] Box320  label="lcdbezelouter002"
  AttacherType = Attacher::AttachEngine3D
  Height = 5
  Length = 61
  Placement = pos=(-55,-2,44) rot=(0,1,0;0.436332rad)
  Width = 200
FEATURE [Part::Box] Box321  label="Cube208"
  AttacherType = Attacher::AttachEngine3D
  Height = 10
  Length = 42
  Placement = pos=(-46,15,42) rot=(0,1,0;0.436332rad)
  Width = 166
FEATURE [Part::Box] Box322  label="lcdbezelouter003"
  AttacherType = Attacher::AttachEngine3D
  Height = 5
  Length = 59
  Placement = pos=(-54,-1,43) rot=(0,1,0;0.436332rad)
  Width = 198
FEATURE [Part::Cut] Cut101
  Base = -> Box320
  Tool = -> Box321
FEATURE [Part::Cut] Cut102  label="LcdBezel001"
  Base = -> Cut101
  Tool = -> Box322
FEATURE [Part::Box] Box323  label="Cube209"
  AttacherType = Attacher::AttachEngine3D
  Height = 2
  Length = 10
  Placement = pos=(0,-2,2.5) rot=(0,0,1;0rad)
  Width = 38
FEATURE [Part::Box] Box324  label="Cube210"
  AttacherType = Attacher::AttachEngine3D
  Height = 2
  Length = 40
  Placement = pos=(0,-1,-6) rot=(0,0,1;0rad)
  Width = 36
FEATURE [Part::Box] Box325  label="Cube211"
  AttacherType = Attacher::AttachEngine3D
  Height = 2.5
  Length = 10
  Placement = pos=(30,-2,2) rot=(0,0,1;0rad)
  Width = 38
FEATURE [Part::Box] Box326  label="Cube212"
  AttacherType = Attacher::AttachEngine3D
  Height = 10.5
  Length = 40
  Placement = pos=(0,-3,-6) rot=(0,0,1;0rad)
  Width = 2
FEATURE [Part::Box] Box327  label="Cube213"
  AttacherType = Attacher::AttachEngine3D
  Height = 10.5
  Length = 40
  Placement = pos=(0,35,-6) rot=(0,0,1;0rad)
  Width = 2
FEATURE [Part::Box] Box328  label="Cube214"
  AttacherType = Attacher::AttachEngine3D
  Height = 8.5
  Length = 2
  Placement = pos=(0,12,-4) rot=(0,0,1;0rad)
  Width = 10
FEATURE [Part::Box] Box329  label="Cube215"
  AttacherType = Attacher::AttachEngine3D
  Height = 2
  Length = 63
  Placement = pos=(2,13,-6) rot=(0,0,1;0rad)
  Width = 10
FEATURE [Part::Box] Box330  label="Cube216"
  AttacherType = Attacher::AttachEngine3D
  Height = 2
  Length = 2
  Placement = pos=(63,13,-5) rot=(0,0,1;0rad)
  Width = 10
FEATURE [Part::MultiFuse] Fusion050  label="batteryholder"
  Placement = pos=(-13,246,-19) rot=(0,0,1;3.14159rad)
  Shapes = -> [Box323,Box324,Box325,Box326,Box327,Box328,Box329,Box330]
FEATURE [Part::Box] Box331  label="lcdbezelouter004"
  AttacherType = Attacher::AttachEngine3D
  Height = 5
  Length = 61
  Placement = pos=(-55,-2,44) rot=(0,1,0;0.436332rad)
  Width = 200
FEATURE [Part::Box] Box332  label="Cube217"
  AttacherType = Attacher::AttachEngine3D
  Height = 10
  Length = 42
  Placement = pos=(-46,15,42) rot=(0,1,0;0.436332rad)
  Width = 166
FEATURE [Part::Box] Box333  label="lcdbezelouter005"
  AttacherType = Attacher::AttachEngine3D
  Height = 5
  Length = 59
  Placement = pos=(-54,-1,43) rot=(0,1,0;0.436332rad)
  Width = 198
FEATURE [Part::Cut] Cut103
  Base = -> Box331
  Tool = -> Box332
FEATURE [Part::Cut] Cut104  label="LcdBezel002"
  Base = -> Cut103
  Tool = -> Box333
FEATURE [App::DocumentObjectGroup] Group015  label="BatteryHolder"
  Group = -> [Fusion050]
FEATURE [Part::Box] Box334  label="Cube218"
  AttacherType = Attacher::AttachEngine3D
  Height = 3
  Length = 85
  Placement = pos=(-83,251,-25) rot=(0,0,1;0rad)
  Width = 3
FEATURE [Part::Box] Box335  label="Cube219"
  AttacherType = Attacher::AttachEngine3D
  Height = 3
  Length = 40
  Placement = pos=(-43,198,15) rot=(0,0,1;0rad)
  Width = 3
FEATURE [Part::Box] Box336  label="Cube220"
  AttacherType = Attacher::AttachEngine3D
  Height = 3
  Length = 23
  Placement = pos=(-83,198,27) rot=(0,0,1;0rad)
  Width = 3
FEATURE [Part::Box] Box337  label="Cube221"
  AttacherType = Attacher::AttachEngine3D
  Height = 34
  Length = 3
  Placement = pos=(-83,198,-15.5) rot=(0,0,1;0rad)
  Width = 3
FEATURE [Part::Box] Box338  label="Cube222"
  AttacherType = Attacher::AttachEngine3D
  Height = 2
  Length = 1
  Placement = pos=(-84,206,-25.5) rot=(0,0,1;0rad)
  Width = 42
FEATURE [Part::Cut] Cut105
  Base = -> Fusion047
  Tool = -> Box338
FEATURE [Part::Cylinder] Cylinder037
  Angle = 360
  AttacherType = Attacher::AttachEngine3D
  FirstAngle = 0
  Height = 2.5
  Placement = pos=(29,127,-27) rot=(0,0,1;0rad)
  Radius = 2
  SecondAngle = 0
FEATURE [Part::Cylinder] Cylinder038
  Angle = 360
  AttacherType = Attacher::AttachEngine3D
  FirstAngle = 0
  Height = 10
  Placement = pos=(-70,127,-29) rot=(0,0,1;0rad)
  Radius = 2
  SecondAngle = 0
FEATURE [Part::Cylinder] Cylinder039
  Angle = 360
  AttacherType = Attacher::AttachEngine3D
  FirstAngle = 0
  Height = 10
  Placement = pos=(-33,127,-29) rot=(0,0,1;0rad)
  Radius = 2
  SecondAngle = 0
FEATURE [Part::Cylinder] Cylinder040
  Angle = 360
  AttacherType = Attacher::AttachEngine3D
  FirstAngle = 0
  Height = 10
  Placement = pos=(29,127,-29) rot=(0,0,1;0rad)
  Radius = 2
  SecondAngle = 0
FEATURE [Part::Cut] Cut106
  Base = -> Cut105
  Tool = -> Cylinder040
FEATURE [Part::Cylinder] Cylinder041
  Angle = 360
  AttacherType = Attacher::AttachEngine3D
  FirstAngle = 0
  Height = 2.5
  Placement = pos=(-33,127,-27) rot=(0,0,1;0rad)
  Radius = 2
  SecondAngle = 0
FEATURE [Part::Cut] Cut107
  Base = -> Fusion046
  Tool = -> Cylinder039
FEATURE [Part::Cylinder] Cylinder042
  Angle = 360
  AttacherType = Attacher::AttachEngine3D
  FirstAngle = 0
  Height = 2.5
  Placement = pos=(-70,127,-27) rot=(0,0,1;0rad)
  Radius = 2
  SecondAngle = 0
FEATURE [Part::Cut] Cut108
  Base = -> Cut107
  Tool = -> Cylinder038
FEATURE [Part::Box] Box339  label="Cube223"
  AttacherType = Attacher::AttachEngine3D
  Height = 2
  Length = 27
  Placement = pos=(-66,127,-25) rot=(0,0,1;0rad)
  Width = 4
FEATURE [Part::Box] Box340  label="Cube224"
  AttacherType = Attacher::AttachEngine3D
  Height = 2
  Length = 36
  Placement = pos=(-13,127,-25) rot=(0,0,1;0rad)
  Width = 4
FEATURE [Part::Box] Box341  label="Cube225"
  AttacherType = Attacher::AttachEngine3D
  Height = 2
  Length = 27
  Placement = pos=(-66,123,-25) rot=(0,0,1;0rad)
  Width = 4
FEATURE [Part::Box] Box342  label="Cube226"
  AttacherType = Attacher::AttachEngine3D
  Height = 2
  Length = 36
  Placement = pos=(-13,123,-25) rot=(0,0,1;0rad)
  Width = 4
FEATURE [Part::Box] Box343  label="Cube227"
  AttacherType = Attacher::AttachEngine3D
  Height = 2
  Length = 2
  Placement = pos=(-83,76,-25) rot=(0,0,1;0rad)
  Width = 51
FEATURE [App::DocumentObjectGroup] Group013  label="LeftSide"
  Group = -> [Cut095,Cylinder034,Cut092,Fusion021,Fusion019,Cylinder037,Cut108,Box342,Box341,Box343]
FEATURE [Part::Box] Box344  label="Lid003"
  AttacherType = Attacher::AttachEngine3D
  Height = 1.5
  Length = 31
  Placement = pos=(-86,-2,44) rot=(0,1,0;0rad)
  Width = 201
FEATURE [Part::Box] Box345  label="Cube228"
  AttacherType = Attacher::AttachEngine3D
  Height = 6
  Length = 23
  Placement = pos=(-80,1,40) rot=(0,0,1;0rad)
  Width = 2
FEATURE [Part::Box] Box346  label="Cube229"
  AttacherType = Attacher::AttachEngine3D
  Height = 6
  Length = 23
  Placement = pos=(-81,194,40) rot=(0,0,1;0rad)
  Width = 2
FEATURE [Part::Box] Box347  label="Cube230"
  AttacherType = Attacher::AttachEngine3D
  Height = 2
  Length = 2
  Placement = pos=(-84.5,60,42) rot=(0,0,1;0rad)
  Width = 80
FEATURE [Part::Box] Box348  label="BoxPanelSupports009"
  AttacherType = Attacher::AttachEngine3D
  Height = 201
  Length = 8
  Placement = pos=(-62,199,45.5) rot=(1,0,0;1.5708rad)
  Width = 1.5
FEATURE [Part::Box] Box349  label="BoxPanelSupports010"
  AttacherType = Attacher::AttachEngine3D
  Height = 201
  Length = 8
  Placement = pos=(-73,199,45.5) rot=(1,0,0;1.5708rad)
  Width = 1.5
FEATURE [Part::Box] Box350  label="BoxPanelSupports011"
  AttacherType = Attacher::AttachEngine3D
  Height = 201
  Length = 8
  Placement = pos=(-84,199,45.5) rot=(1,0,0;1.5708rad)
  Width = 1.5
FEATURE [Part::MultiFuse] Fusion051
  Placement = pos=(9,0,15) rot=(0,-1,0;0.261799rad)
  Shapes = -> [Box344,Box345,Box346,Box347,Box348,Box349,Box350]
FEATURE [App::DocumentObjectGroup] Group016  label="NewLid"
  Group = -> [Fusion051]
FEATURE [Part::Box] Box351  label="Cube231"
  AttacherType = Attacher::AttachEngine3D
  Height = 26
  Length = 21
  Placement = pos=(-38,191,-13) rot=(0,0,1;0rad)
  Width = 10
FEATURE [Part::Cut] Cut109
  Base = -> Cut037
  Tool = -> Box351
FEATURE [App::DocumentObjectGroup] Group011  label="RightSide"
  Group = -> [Cut098,Cut100,Cut052,Cut093,Cylinder036,Box334,Box335,Box336,Box337,Box213,Cut106,Cylinder041,Cylinder042,Box339,Box340,Cut109]
FEATURE [Part::Box] Box352  label="extcartdupont"
  AttacherType = Attacher::AttachEngine3D
  Height = 3
  Length = 10
  Placement = pos=(0,9,5) rot=(0,0,1;0rad)
  Width = 31
FEATURE [Part::Cut] Cut
  Base = -> Box054
  Tool = -> Box004
FEATURE [Part::Cut] Cut110
  Base = -> Cut
  Tool = -> Box352
FEATURE [Part::Box] Box353  label="Cube232"
  AttacherType = Attacher::AttachEngine3D
  Height = 2
  Length = 4
  Placement = pos=(1,7,3) rot=(0,0,1;0rad)
  Width = 35
FEATURE [Part::MultiFuse] Fusion011
  Placement = pos=(-86,1,-6.5) rot=(0,0,1;0rad)
  Shapes = -> [Box025,Box026,Cut110,Box353]
FEATURE [Part::Box] Box354  label="powerswitch"
  AttacherType = Attacher::AttachEngine3D
  Height = 8
  Length = 16
  Placement = pos=(-92,219,1) rot=(0,1,0;0rad)
  Width = 16
FEATURE [Part::Box] Box355  label="PowerPanelPlate"
  AttacherType = Attacher::AttachEngine3D
  Height = 57
  Length = 2
  Placement = pos=(-85,199.5,-24.5) rot=(0,0,1;0rad)
  Width = 54
FEATURE [Part::Box] Box356  label="usbsocket"
  AttacherType = Attacher::AttachEngine3D
  Height = 3.5
  Length = 16
  Placement = pos=(-92,223,-11) rot=(0,1,0;0rad)
  Width = 8
FEATURE [Part::Box] Box357  label="chargerplate1"
  AttacherType = Attacher::AttachEngine3D
  Height = 2
  Length = 16
  Placement = pos=(-84,216,-14.6) rot=(0,1,0;0rad)
  Width = 22
FEATURE [Part::Box] Box358  label="chargerplate002"
  AttacherType = Attacher::AttachEngine3D
  Height = 2
  Length = 5
  Placement = pos=(-84,216,-11) rot=(0,1,0;0rad)
  Width = 22
FEATURE [Part::Box] Box359  label="Cube233"
  AttacherType = Attacher::AttachEngine3D
  Height = 5
  Length = 5
  Placement = pos=(-84,201.5,10) rot=(0,0,1;0rad)
  Width = 3
FEATURE [Part::Box] Box360  label="Cube234"
  AttacherType = Attacher::AttachEngine3D
  Height = 5
  Length = 5
  Placement = pos=(-84,248.5,10) rot=(0,0,1;0rad)
  Width = 3
FEATURE [Part::Box] Box361  label="Cube235"
  AttacherType = Attacher::AttachEngine3D
  Height = 5
  Length = 3
  Placement = pos=(-79.7,248.5,10) rot=(0,0,1;0rad)
  Width = 5
FEATURE [Part::Box] Box362  label="Cube236"
  AttacherType = Attacher::AttachEngine3D
  Height = 5
  Length = 3
  Placement = pos=(-79.7,199.5,10) rot=(0,0,1;0rad)
  Width = 5
FEATURE [Part::MultiFuse] Fusion052
  Shapes = -> [Box355,Box357,Box358,Box359,Box360,Box361,Box362]
FEATURE [Part::Cut] Cut111
  Base = -> Fusion052
  Tool = -> Box356
FEATURE [Part::Cut] Cut112
  Base = -> Cut111
  Tool = -> Box354
FEATURE [Part::Cylinder] Cylinder044  label="screwhole"
  Angle = 360
  AttacherType = Attacher::AttachEngine3D
  FirstAngle = 0
  Height = 20
  Placement = pos=(-91,227,28) rot=(0,1,0;1.5708rad)
  Radius = 1.5
  SecondAngle = 0
FEATURE [Part::Cut] Cut113
  Base = -> Cut112
  Tool = -> Cylinder044
FEATURE [Part::Box] Box363  label="usbinset"
  AttacherType = Attacher::AttachEngine3D
  Height = 10
  Length = 10
  Placement = pos=(-94,219,-14) rot=(0,0,1;0rad)
  Width = 15.5
FEATURE [Part::Cut] Cut114
  Base = -> Cut113
  Tool = -> Box363
FEATURE [App::DocumentObjectGroup] Group017  label="PowerPanel"
  Group = -> [Cut114]
FEATURE [Part::Cylinder] Cylinder043  label="resetbutton001"
  Angle = 360
  AttacherType = Attacher::AttachEngine3D
  FirstAngle = 0
  Height = 10
  Placement = pos=(-86,177,0) rot=(0,1,0;1.5708rad)
  Radius = 4.2
  SecondAngle = 0
FEATURE [Part::Cut] Cut115
  Base = -> Fusion011
  Tool = -> Cylinder043
FEATURE [App::DocumentObjectGroup] Group002  label="Back"
  Group = -> [Cut115]
FEATURE [Part::Box] Box364  label="Cube237"
  AttacherType = Attacher::AttachEngine3D
  Height = 7
  Length = 20
  Placement = pos=(150,124,0) rot=(0,0,1;0rad)
  Width = 3
FEATURE [Part::MultiFuse] Fusion042
  Shapes = -> [Box243,Box244,Box246,Box247,Box248,Box249,Box250,Box364]
FEATURE [Part::Cut] Cut081
  Base = -> Fusion042
  Tool = -> Cylinder018
FEATURE [Part::Cut] Cut082  label="KeyboardBezelLeft"
  Base = -> Cut081
  Tool = -> Cylinder017
FEATURE [Part::Cylinder] Cylinder045  label="Cylinder045-screwspace"
  Angle = 360
  AttacherType = Attacher::AttachEngine3D
  FirstAngle = 0
  Height = 5
  Placement = pos=(156,9,2) rot=(0,0,1;0rad)
  Radius = 3.5
  SecondAngle = 0
FEATURE [Part::Cylinder] Cylinder046  label="Cylinder046-screwspace"
  Angle = 360
  AttacherType = Attacher::AttachEngine3D
  FirstAngle = 0
  Height = 5
  Placement = pos=(248,9,2) rot=(0,0,1;0rad)
  Radius = 3.5
  SecondAngle = 0
FEATURE [Part::Cut] Cut116
  Base = -> Cut082
  Tool = -> Cylinder045
FEATURE [Part::Cut] Cut117
  Base = -> Cut116
  Placement = pos=(0,79,0) rot=(0,0,1;0rad)
  Tool = -> Cylinder046
FEATURE [App::DocumentObjectGroup] Group018  label="KeyboardLeftBez"
  Group = -> [Cut117]
FEATURE [Part::Box] Box365  label="Cube238"
  AttacherType = Attacher::AttachEngine3D
  Height = 2
  Length = 23
  Placement = pos=(231,14,7) rot=(0,0,1;0rad)
  Width = 36
FEATURE [Part::Box] Box366  label="Cube239"
  AttacherType = Attacher::AttachEngine3D
  Height = 7
  Length = 15
  Placement = pos=(239,48,0) rot=(0,0,1;0rad)
  Width = 2
FEATURE [Part::MultiFuse] Fusion045
  Shapes = -> [Box268,Box269,Box270,Box271,Box273,Box274,Box276,Box277,Cut089,Box365,Box366]
FEATURE [Part::Cut] Cut085
  Base = -> Fusion045
  Tool = -> Cylinder030
FEATURE [Part::Cut] Cut086  label="KeyboardBezelRight"
  Base = -> Cut085
  Tool = -> Cylinder029
FEATURE [Part::Cylinder] Cylinder047
  Angle = 360
  AttacherType = Attacher::AttachEngine3D
  FirstAngle = 0
  Height = 10
  Placement = pos=(158,8,2) rot=(0,0,1;0rad)
  Radius = 3.5
  SecondAngle = 0
FEATURE [Part::Cylinder] Cylinder048
  Angle = 360
  AttacherType = Attacher::AttachEngine3D
  FirstAngle = 0
  Height = 10
  Placement = pos=(248,8,2) rot=(0,0,1;0rad)
  Radius = 3.5
  SecondAngle = 0
FEATURE [Part::Cut] Cut118
  Base = -> Cut086
  Tool = -> Cylinder047
FEATURE [Part::Cut] Cut119
  Base = -> Cut118
  Tool = -> Cylinder048
FEATURE [Part::Box] Box367  label="Cube240"
  AttacherType = Attacher::AttachEngine3D
  Height = 2
  Length = 23
  Placement = pos=(236,15,0) rot=(0,0,1;0rad)
  Width = 33
FEATURE [Part::Cut] Cut120
  Base = -> Cut119
  Tool = -> Box367
FEATURE [App::DocumentObjectGroup] Group019  label="KeyboardRIghtBez"
  Group = -> [Cut120]
